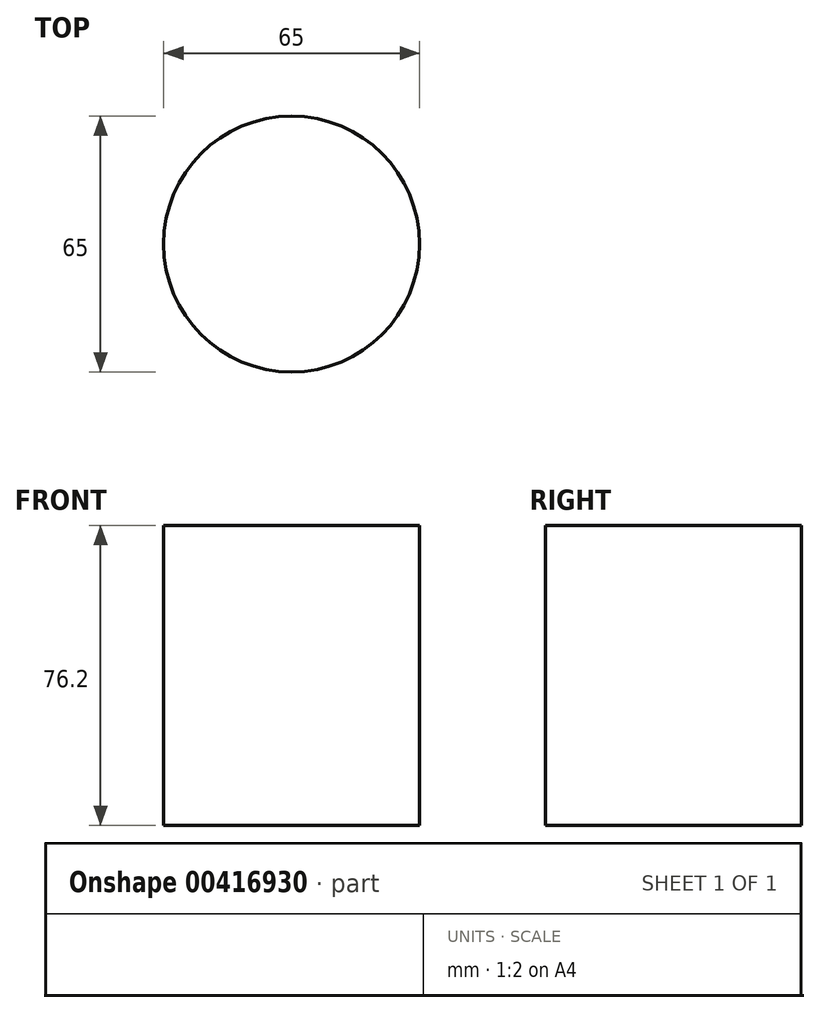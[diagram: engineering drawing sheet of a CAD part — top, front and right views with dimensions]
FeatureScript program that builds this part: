
annotation { "Feature Type Name" : "Feature", "Feature Type Description" : "" }
export const myFeature = defineFeature(function(context is Context, id is Id, definition is map)
    precondition{}
    {
        {
            var Q0;
            Q0=qCreatedBy(makeId("Top.planeOp"),FACE);
            var sketch = newSketch(context, id + "F0", { "sketchPlane" : qUnion([Q0])});
            skCircle(sketch, "E0", {"center": v(0, 0) * mm, "radius": 32.5 * mm});
            skSolve(sketch);
        }
        {
            var Q0;
            Q0=makeQuery(id+"F0.imprint","IMPRINT",FACE,{"disambiguationData":[TD([[makeQuery(id+"F0.imprint","IMPRINT",EDGE,{"derivedFrom":sQuery(id+"F0.wireOp",EDGE,"E0")}),1.0]])]});
            extrude(context, id + "F1", {"entities" : qUnion([Q0]), "depth" : 76.2 * mm});
        }
    });
